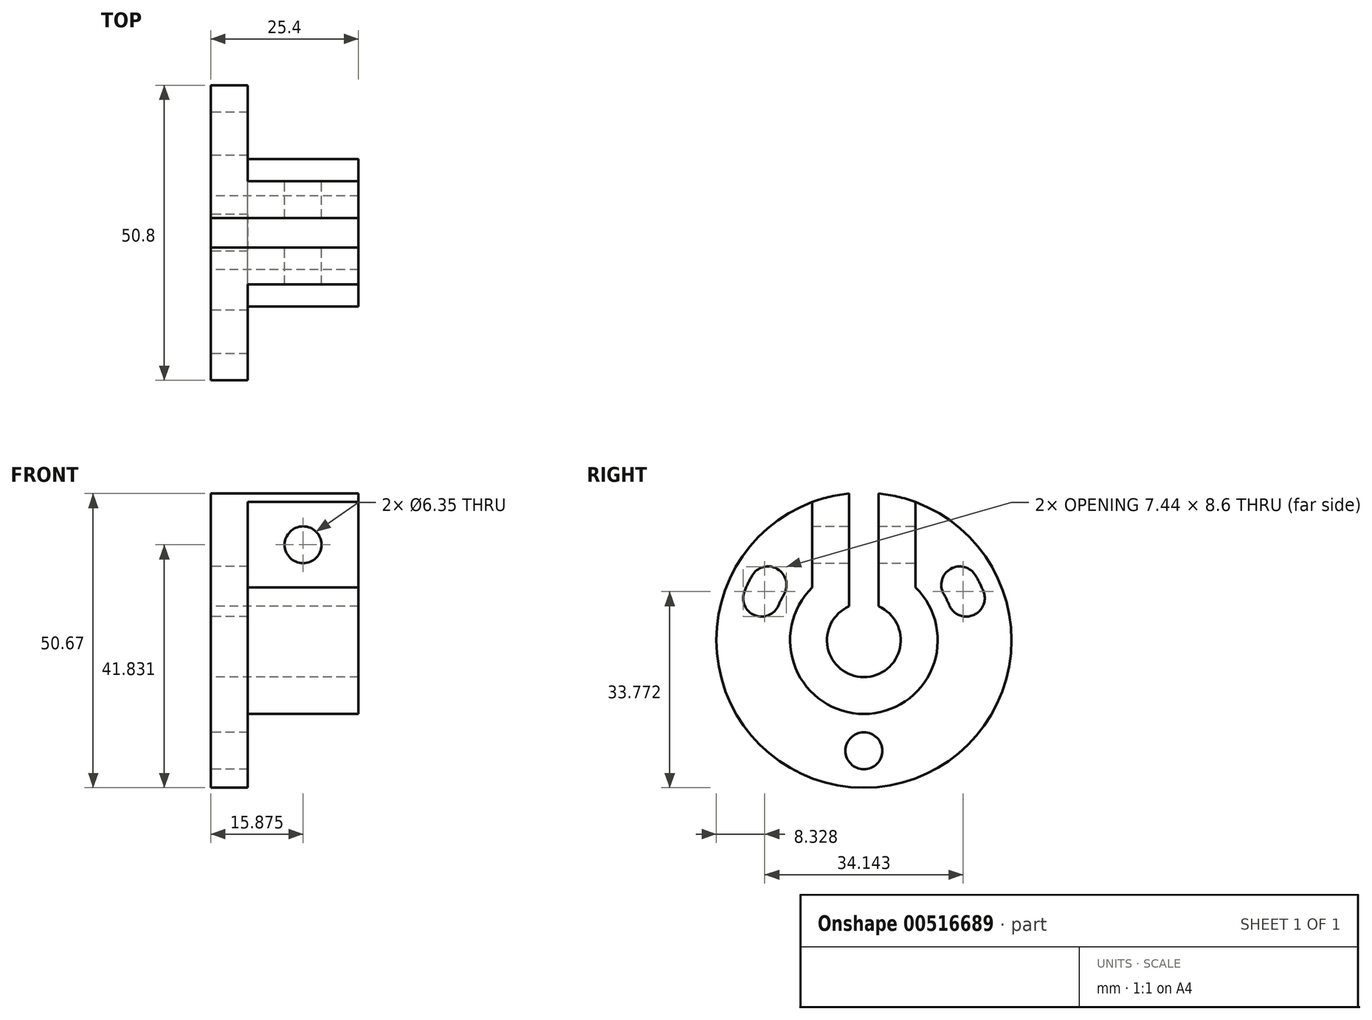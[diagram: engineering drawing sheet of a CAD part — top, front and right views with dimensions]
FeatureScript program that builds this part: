
annotation { "Feature Type Name" : "Feature", "Feature Type Description" : "" }
export const myFeature = defineFeature(function(context is Context, id is Id, definition is map)
    precondition{}
    {
        {
            var Q0;
            Q0=qCreatedBy(makeId("Right.planeOp"),FACE);
            var sketch = newSketch(context, id + "F0", { "sketchPlane" : qUnion([Q0])});
            skCircle(sketch, "E0", {"center": v(0, 0) * mm, "radius": 6.35 * mm});
            skCircle(sketch, "E1", {"center": v(0, 0) * mm, "radius": 12.7 * mm});
            skCircle(sketch, "E2", {"center": v(0, 0) * mm, "radius": 25.4 * mm});
            skLineSegment(sketch, "E3.top", {"start": v(8.89, 23.8) * mm, "end": v(-8.89, 23.8) * mm});
            skLineSegment(sketch, "E3.left", {"start": v(8.9, 0) * mm, "end": v(8.9, 23.8) * mm});
            skLineSegment(sketch, "E3.right", {"start": v(-8.9, 0) * mm, "end": v(-8.9, 23.8) * mm});
            skLineSegment(sketch, "E4.bottom", {"start": v(2.54, 0) * mm, "end": v(-2.54, 0) * mm});
            skLineSegment(sketch, "E4.top", {"start": v(2.54, 25.27) * mm, "end": v(-2.54, 25.27) * mm});
            skLineSegment(sketch, "E4.left", {"start": v(2.54, 0) * mm, "end": v(2.54, 25.27) * mm});
            skLineSegment(sketch, "E4.right", {"start": v(-2.54, 0) * mm, "end": v(-2.54, 25.27) * mm});
            skCircle(sketch, "E5", {"center": v(-16.5, 9.53) * mm, "radius": 3.18 * mm});
            skCircle(sketch, "E6", {"center": v(0, -19.05) * mm, "radius": 3.18 * mm});
            skCircle(sketch, "E7", {"center": v(16.5, 9.53) * mm, "radius": 3.18 * mm});
            skCircle(sketch, "E8.cCircle", {"center": v(0, 0) * mm, "radius": 19.05 * mm, "construction": true});
            skLineSegment(sketch, "E8.0", {"start": v(-16.5, 9.53) * mm, "end": v(16.5, 9.53) * mm, "construction": true});
            skLineSegment(sketch, "E8.1", {"start": v(16.5, 9.53) * mm, "end": v(0, -19.05) * mm, "construction": true});
            skLineSegment(sketch, "E8.2", {"start": v(0, -19.05) * mm, "end": v(-16.5, 9.52) * mm, "construction": true});
            skLineSegment(sketch, "E9", {"start": v(-8.9, 0) * mm, "end": v(8.9, 0) * mm});
            skCircle(sketch, "E10", {"center": v(-17.62, 7.25) * mm, "radius": 3.18 * mm});
            skCircle(sketch, "E11", {"center": v(17.62, 7.25) * mm, "radius": 3.18 * mm});
            skCircle(sketch, "E12", {"center": v(0, 0) * mm, "radius": 22.23 * mm});
            skCircle(sketch, "E13", {"center": v(0, 0) * mm, "radius": 15.88 * mm});
            skSolve(sketch);
        }
        {
            var Q0;
            Q0=makeQuery(id+"F0.imprint","IMPRINT",FACE,{"disambiguationData":[TD([[makeQuery(id+"F0.imprint","IMPRINT",EDGE,{"derivedFrom":sQuery(id+"F0.wireOp",EDGE,"E6")}),-1.0]])]});
            var Q1;
            {var subQ0=sQuery(id+"F0.wireOp",EDGE,"E3.left");var subQ1=sQuery(id+"F0.wireOp",EDGE,"E1");var subQ2=makeQuery(id+"F0.imprint","INTERSECT",VERTEX,{"derivedFrom":[subQ1,subQ0]});Q1=makeQuery(id+"F0.imprint","IMPRINT",FACE,{"disambiguationData":[TD([[makeQuery(id+"F0.imprint","IMPRINT",EDGE,{"disambiguationData":[TD([[subQ2,-1.0]])],"derivedFrom":subQ1}),-1.0]])]});}
            var Q2;
            {var subQ0=sQuery(id+"F0.wireOp",EDGE,"E3.top");var subQ3=sQuery(id+"F0.wireOp",EDGE,"E4.left");var subQ5=makeQuery(id+"F0.imprint","INTERSECT",VERTEX,{"derivedFrom":[subQ0,subQ3]});Q2=makeQuery(id+"F0.imprint","IMPRINT",FACE,{"disambiguationData":[TD([[makeQuery(id+"F0.imprint","IMPRINT",EDGE,{"disambiguationData":[TD([[subQ5,1.0]])],"derivedFrom":subQ0}),-1.0]])]});}
            var Q3;
            {var subQ0=sQuery(id+"F0.wireOp",EDGE,"E3.top");var subQ3=sQuery(id+"F0.wireOp",EDGE,"E4.right");var subQ5=makeQuery(id+"F0.imprint","INTERSECT",VERTEX,{"derivedFrom":[subQ0,subQ3]});Q3=makeQuery(id+"F0.imprint","IMPRINT",FACE,{"disambiguationData":[TD([[makeQuery(id+"F0.imprint","IMPRINT",EDGE,{"disambiguationData":[TD([[subQ5,-1.0]])],"derivedFrom":subQ0}),-1.0]])]});}
            var Q4;
            {var subQ0=sQuery(id+"F0.wireOp",EDGE,"E3.right");var subQ5=sQuery(id+"F0.wireOp",EDGE,"E1");var subQ6=makeQuery(id+"F0.imprint","INTERSECT",VERTEX,{"derivedFrom":[subQ5,subQ0]});Q4=makeQuery(id+"F0.imprint","IMPRINT",FACE,{"disambiguationData":[TD([[makeQuery(id+"F0.imprint","IMPRINT",EDGE,{"disambiguationData":[TD([[subQ6,1.0]])],"derivedFrom":subQ5}),-1.0]])]});}
            var Q5;
            {var subQ0=sQuery(id+"F0.wireOp",EDGE,"E4.right");var subQ1=sQuery(id+"F0.wireOp",EDGE,"E0");var subQ2=makeQuery(id+"F0.imprint","INTERSECT",VERTEX,{"derivedFrom":[subQ1,subQ0]});Q5=makeQuery(id+"F0.imprint","IMPRINT",FACE,{"disambiguationData":[TD([[makeQuery(id+"F0.imprint","IMPRINT",EDGE,{"disambiguationData":[TD([[subQ2,-1.0]])],"derivedFrom":subQ1}),-1.0]])]});}
            var Q6;
            {var subQ0=sQuery(id+"F0.wireOp",EDGE,"E9");var subQ8=sQuery(id+"F0.wireOp",EDGE,"E0");var subQ9=makeQuery(id+"F0.imprint","INTERSECT",VERTEX,{"disambiguationData":[OD(0.0)],"derivedFrom":[subQ8,subQ0]});Q6=makeQuery(id+"F0.imprint","IMPRINT",FACE,{"disambiguationData":[TD([[makeQuery(id+"F0.imprint","IMPRINT",EDGE,{"disambiguationData":[TD([[subQ9,1.0]])],"derivedFrom":subQ8}),-1.0]])]});}
            var Q7;
            {var subQ0=sQuery(id+"F0.wireOp",EDGE,"E4.left");var subQ1=sQuery(id+"F0.wireOp",EDGE,"E0");var subQ2=makeQuery(id+"F0.imprint","INTERSECT",VERTEX,{"derivedFrom":[subQ1,subQ0]});Q7=makeQuery(id+"F0.imprint","IMPRINT",FACE,{"disambiguationData":[TD([[makeQuery(id+"F0.imprint","IMPRINT",EDGE,{"disambiguationData":[TD([[subQ2,1.0]])],"derivedFrom":subQ1}),-1.0]])]});}
            var Q8;
            {var subQ0=sQuery(id+"F0.wireOp",EDGE,"E13");var subQ1=sQuery(id+"F0.wireOp",EDGE,"E3.right");var subQ2=makeQuery(id+"F0.imprint","INTERSECT",VERTEX,{"derivedFrom":[subQ1,subQ0]});Q8=makeQuery(id+"F0.imprint","IMPRINT",FACE,{"disambiguationData":[TD([[makeQuery(id+"F0.imprint","IMPRINT",EDGE,{"disambiguationData":[TD([[subQ2,-1.0]])],"derivedFrom":subQ1}),1.0]])]});}
            var Q9;
            {var subQ4=sQuery(id+"F0.wireOp",EDGE,"E1");var subQ9=sQuery(id+"F0.wireOp",EDGE,"E3.left");var subQ10=makeQuery(id+"F0.imprint","INTERSECT",VERTEX,{"derivedFrom":[subQ4,subQ9]});Q9=makeQuery(id+"F0.imprint","IMPRINT",FACE,{"disambiguationData":[TD([[makeQuery(id+"F0.imprint","IMPRINT",EDGE,{"disambiguationData":[TD([[subQ10,1.0]])],"derivedFrom":subQ4}),-1.0]])]});}
            var Q10;
            {var subQ0=sQuery(id+"F0.wireOp",EDGE,"E12");var subQ1=makeQuery(id+"F0.imprint","INTERSECT",VERTEX,{"derivedFrom":[sQuery(id+"F0.wireOp",EDGE,"E7"),subQ0]});Q10=makeQuery(id+"F0.imprint","IMPRINT",FACE,{"disambiguationData":[TD([[makeQuery(id+"F0.imprint","IMPRINT",EDGE,{"disambiguationData":[TD([[subQ1,1.0]])],"derivedFrom":subQ0}),-1.0]])]});}
            var Q11;
            {var subQ1=sQuery(id+"F0.wireOp",EDGE,"E3.top");var subQ3=sQuery(id+"F0.wireOp",EDGE,"E4.right");var subQ4=makeQuery(id+"F0.imprint","INTERSECT",VERTEX,{"derivedFrom":[subQ1,subQ3]});Q11=makeQuery(id+"F0.imprint","IMPRINT",FACE,{"disambiguationData":[TD([[makeQuery(id+"F0.imprint","IMPRINT",EDGE,{"disambiguationData":[TD([[subQ4,1.0]])],"derivedFrom":subQ3}),1.0]])]});}
            var Q12;
            {var subQ0=sQuery(id+"F0.wireOp",EDGE,"E13");var subQ1=sQuery(id+"F0.wireOp",EDGE,"E3.right");var subQ2=makeQuery(id+"F0.imprint","INTERSECT",VERTEX,{"derivedFrom":[subQ1,subQ0]});Q12=makeQuery(id+"F0.imprint","IMPRINT",FACE,{"disambiguationData":[TD([[makeQuery(id+"F0.imprint","IMPRINT",EDGE,{"disambiguationData":[TD([[subQ2,-1.0]])],"derivedFrom":subQ1}),-1.0]])]});}
            var Q13;
            {var subQ0=sQuery(id+"F0.wireOp",EDGE,"E13");var subQ1=sQuery(id+"F0.wireOp",EDGE,"E3.left");var subQ2=makeQuery(id+"F0.imprint","INTERSECT",VERTEX,{"derivedFrom":[subQ1,subQ0]});Q13=makeQuery(id+"F0.imprint","IMPRINT",FACE,{"disambiguationData":[TD([[makeQuery(id+"F0.imprint","IMPRINT",EDGE,{"disambiguationData":[TD([[subQ2,-1.0]])],"derivedFrom":subQ1}),1.0]])]});}
            var Q14;
            {var subQ1=sQuery(id+"F0.wireOp",EDGE,"E3.top");var subQ3=sQuery(id+"F0.wireOp",EDGE,"E4.left");var subQ4=makeQuery(id+"F0.imprint","INTERSECT",VERTEX,{"derivedFrom":[subQ1,subQ3]});Q14=makeQuery(id+"F0.imprint","IMPRINT",FACE,{"disambiguationData":[TD([[makeQuery(id+"F0.imprint","IMPRINT",EDGE,{"disambiguationData":[TD([[subQ4,1.0]])],"derivedFrom":subQ3}),-1.0]])]});}
            var Q15;
            {var subQ0=sQuery(id+"F0.wireOp",EDGE,"E13");var subQ1=sQuery(id+"F0.wireOp",EDGE,"E3.left");var subQ2=makeQuery(id+"F0.imprint","INTERSECT",VERTEX,{"derivedFrom":[subQ1,subQ0]});Q15=makeQuery(id+"F0.imprint","IMPRINT",FACE,{"disambiguationData":[TD([[makeQuery(id+"F0.imprint","IMPRINT",EDGE,{"disambiguationData":[TD([[subQ2,-1.0]])],"derivedFrom":subQ1}),-1.0]])]});}
            extrude(context, id + "F1", {"entities" : qUnion([Q0, Q1, Q2, Q3, Q4, Q5, Q6, Q7, Q8, Q9, Q10, Q11, Q12, Q13, Q14, Q15]), "depth" : 6.35 * mm, "offsetDistance" : 25.4 * mm});
        }
        {
            var Q0;
            {var subQ5=sQuery(id+"F0.wireOp",EDGE,"E0");var subQ7=sQuery(id+"F0.wireOp",EDGE,"E4.left");var subQ9=makeQuery(id+"F0.imprint","INTERSECT",VERTEX,{"derivedFrom":[subQ5,subQ7]});Q0=makeQuery(id+"F0.imprint","IMPRINT",FACE,{"disambiguationData":[TD([[makeQuery(id+"F0.imprint","IMPRINT",EDGE,{"disambiguationData":[TD([[subQ9,1.0]])],"derivedFrom":subQ5}),-1.0]])]});}
            var Q1;
            {var subQ0=sQuery(id+"F0.wireOp",EDGE,"E3.left");var subQ1=sQuery(id+"F0.wireOp",EDGE,"E1");var subQ2=makeQuery(id+"F0.imprint","INTERSECT",VERTEX,{"derivedFrom":[subQ1,subQ0]});Q1=makeQuery(id+"F0.imprint","IMPRINT",FACE,{"disambiguationData":[TD([[makeQuery(id+"F0.imprint","IMPRINT",EDGE,{"disambiguationData":[TD([[subQ2,-1.0]])],"derivedFrom":subQ1}),-1.0]])]});}
            var Q2;
            {var subQ0=sQuery(id+"F0.wireOp",EDGE,"E3.right");var subQ5=sQuery(id+"F0.wireOp",EDGE,"E1");var subQ6=makeQuery(id+"F0.imprint","INTERSECT",VERTEX,{"derivedFrom":[subQ5,subQ0]});Q2=makeQuery(id+"F0.imprint","IMPRINT",FACE,{"disambiguationData":[TD([[makeQuery(id+"F0.imprint","IMPRINT",EDGE,{"disambiguationData":[TD([[subQ6,1.0]])],"derivedFrom":subQ5}),-1.0]])]});}
            var Q3;
            {var subQ0=sQuery(id+"F0.wireOp",EDGE,"E4.right");var subQ1=sQuery(id+"F0.wireOp",EDGE,"E0");var subQ2=makeQuery(id+"F0.imprint","INTERSECT",VERTEX,{"derivedFrom":[subQ1,subQ0]});Q3=makeQuery(id+"F0.imprint","IMPRINT",FACE,{"disambiguationData":[TD([[makeQuery(id+"F0.imprint","IMPRINT",EDGE,{"disambiguationData":[TD([[subQ2,-1.0]])],"derivedFrom":subQ1}),-1.0]])]});}
            var Q4;
            {var subQ0=sQuery(id+"F0.wireOp",EDGE,"E9");var subQ8=sQuery(id+"F0.wireOp",EDGE,"E0");var subQ9=makeQuery(id+"F0.imprint","INTERSECT",VERTEX,{"disambiguationData":[OD(0.0)],"derivedFrom":[subQ8,subQ0]});Q4=makeQuery(id+"F0.imprint","IMPRINT",FACE,{"disambiguationData":[TD([[makeQuery(id+"F0.imprint","IMPRINT",EDGE,{"disambiguationData":[TD([[subQ9,1.0]])],"derivedFrom":subQ8}),-1.0]])]});}
            var Q5;
            {var subQ0=sQuery(id+"F0.wireOp",EDGE,"E3.top");var subQ3=sQuery(id+"F0.wireOp",EDGE,"E4.right");var subQ5=makeQuery(id+"F0.imprint","INTERSECT",VERTEX,{"derivedFrom":[subQ0,subQ3]});Q5=makeQuery(id+"F0.imprint","IMPRINT",FACE,{"disambiguationData":[TD([[makeQuery(id+"F0.imprint","IMPRINT",EDGE,{"disambiguationData":[TD([[subQ5,-1.0]])],"derivedFrom":subQ0}),-1.0]])]});}
            var Q6;
            {var subQ0=sQuery(id+"F0.wireOp",EDGE,"E3.top");var subQ3=sQuery(id+"F0.wireOp",EDGE,"E4.left");var subQ5=makeQuery(id+"F0.imprint","INTERSECT",VERTEX,{"derivedFrom":[subQ0,subQ3]});Q6=makeQuery(id+"F0.imprint","IMPRINT",FACE,{"disambiguationData":[TD([[makeQuery(id+"F0.imprint","IMPRINT",EDGE,{"disambiguationData":[TD([[subQ5,1.0]])],"derivedFrom":subQ0}),-1.0]])]});}
            var Q7;
            {var subQ0=sQuery(id+"F0.wireOp",EDGE,"E13");var subQ1=sQuery(id+"F0.wireOp",EDGE,"E3.right");var subQ2=makeQuery(id+"F0.imprint","INTERSECT",VERTEX,{"derivedFrom":[subQ1,subQ0]});Q7=makeQuery(id+"F0.imprint","IMPRINT",FACE,{"disambiguationData":[TD([[makeQuery(id+"F0.imprint","IMPRINT",EDGE,{"disambiguationData":[TD([[subQ2,-1.0]])],"derivedFrom":subQ1}),-1.0]])]});}
            var Q8;
            {var subQ1=sQuery(id+"F0.wireOp",EDGE,"E3.top");var subQ3=sQuery(id+"F0.wireOp",EDGE,"E4.right");var subQ4=makeQuery(id+"F0.imprint","INTERSECT",VERTEX,{"derivedFrom":[subQ1,subQ3]});Q8=makeQuery(id+"F0.imprint","IMPRINT",FACE,{"disambiguationData":[TD([[makeQuery(id+"F0.imprint","IMPRINT",EDGE,{"disambiguationData":[TD([[subQ4,1.0]])],"derivedFrom":subQ3}),1.0]])]});}
            var Q9;
            {var subQ0=sQuery(id+"F0.wireOp",EDGE,"E13");var subQ1=sQuery(id+"F0.wireOp",EDGE,"E3.left");var subQ2=makeQuery(id+"F0.imprint","INTERSECT",VERTEX,{"derivedFrom":[subQ1,subQ0]});Q9=makeQuery(id+"F0.imprint","IMPRINT",FACE,{"disambiguationData":[TD([[makeQuery(id+"F0.imprint","IMPRINT",EDGE,{"disambiguationData":[TD([[subQ2,-1.0]])],"derivedFrom":subQ1}),1.0]])]});}
            var Q10;
            {var subQ1=sQuery(id+"F0.wireOp",EDGE,"E3.top");var subQ3=sQuery(id+"F0.wireOp",EDGE,"E4.left");var subQ4=makeQuery(id+"F0.imprint","INTERSECT",VERTEX,{"derivedFrom":[subQ1,subQ3]});Q10=makeQuery(id+"F0.imprint","IMPRINT",FACE,{"disambiguationData":[TD([[makeQuery(id+"F0.imprint","IMPRINT",EDGE,{"disambiguationData":[TD([[subQ4,1.0]])],"derivedFrom":subQ3}),-1.0]])]});}
            extrude(context, id + "F2", {"entities" : qUnion([Q0, Q1, Q2, Q3, Q4, Q5, Q6, Q7, Q8, Q9, Q10]), "operationType" : NewBodyOperationType.ADD, "depth" : 25.4 * mm, "offsetDistance" : 25.4 * mm});
        }
        {
            var Q0;
            Q0=makeQuery(id+"F2.opExtrude","SWEPT_FACE",FACE,{"disambiguationData":[OSD([sQuery(id+"F0.wireOp",EDGE,"E3.left")])]});
            var sketch = newSketch(context, id + "F3", { "sketchPlane" : qUnion([Q0])});
            skCircle(sketch, "E14", {"center": v(-15.88, 16.43) * mm, "radius": 3.18 * mm});
            skSolve(sketch);
        }
        {
            var Q0;
            Q0=makeQuery(id+"F3.imprint","IMPRINT",FACE,{"disambiguationData":[TD([[makeQuery(id+"F3.imprint","IMPRINT",EDGE,{"derivedFrom":sQuery(id+"F3.wireOp",EDGE,"E14")}),1.0]])]});
            var Q1;
            Q1=makeQuery(id+"F2.opExtrude","SWEPT_FACE",FACE,{"disambiguationData":[OSD([sQuery(id+"F0.wireOp",EDGE,"E3.right")])]});
            extrude(context, id + "F4", {"entities" : qUnion([Q0]), "operationType" : NewBodyOperationType.REMOVE, "endBound" : BoundingType.UP_TO_SURFACE, "oppositeDirection" : true, "depth" : 25.4 * mm, "endBoundEntityFace" : qUnion([Q1]), "offsetDistance" : 25.4 * mm});
        }
    });
